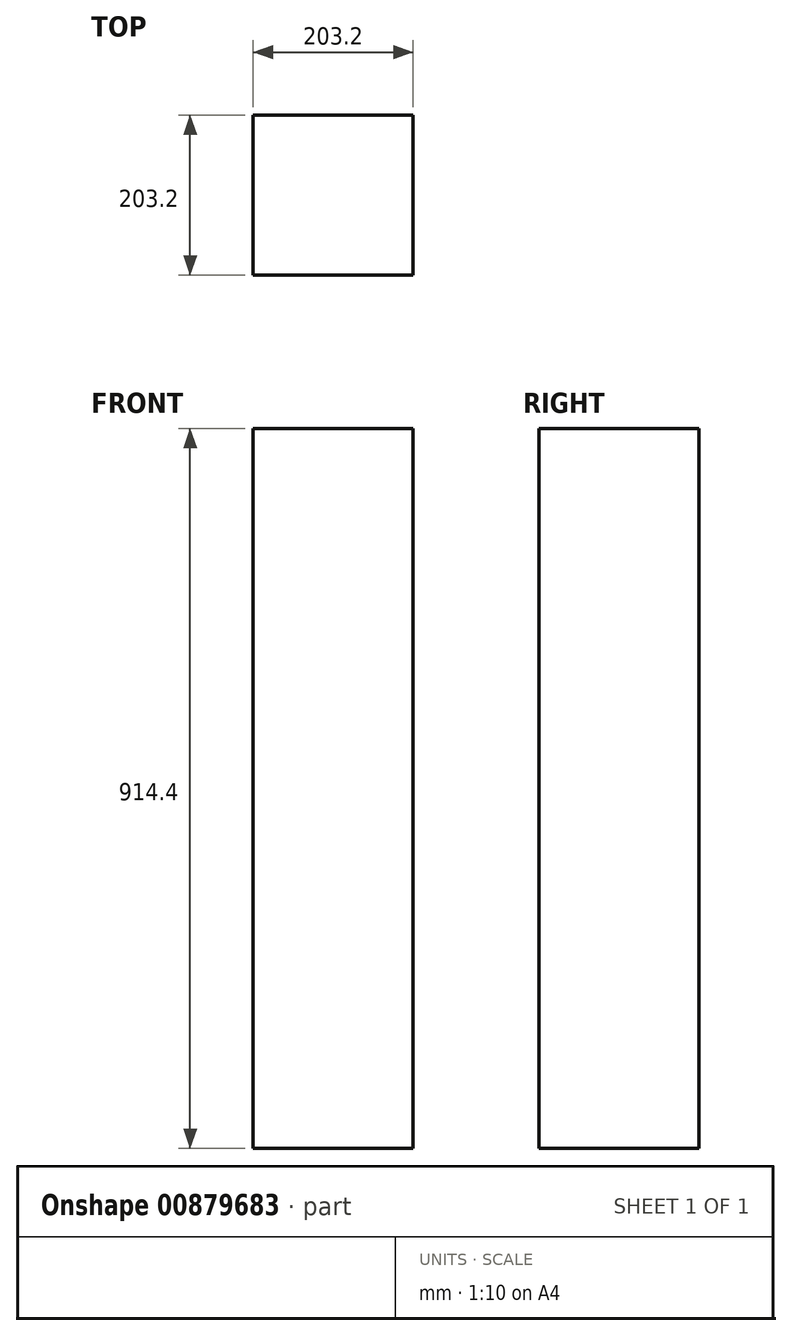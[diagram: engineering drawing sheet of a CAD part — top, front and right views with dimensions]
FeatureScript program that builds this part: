
annotation { "Feature Type Name" : "Feature", "Feature Type Description" : "" }
export const myFeature = defineFeature(function(context is Context, id is Id, definition is map)
    precondition{}
    {
        {
            var Q0;
            Q0=qCreatedBy(makeId("Top.planeOp"),FACE);
            var sketch = newSketch(context, id + "F0", { "sketchPlane" : qUnion([Q0])});
            skLineSegment(sketch, "E0.bottom", {"start": v(-99.17, 115.85) * mm, "end": v(104.03, 115.85) * mm});
            skLineSegment(sketch, "E0.top", {"start": v(-99.17, -87.35) * mm, "end": v(104.03, -87.35) * mm});
            skLineSegment(sketch, "E0.left", {"start": v(-99.17, 115.85) * mm, "end": v(-99.17, -87.35) * mm});
            skLineSegment(sketch, "E0.right", {"start": v(104.03, 115.85) * mm, "end": v(104.03, -87.35) * mm});
            skSolve(sketch);
        }
        {
            var Q0;
            Q0=makeQuery(id+"F0.imprint","IMPRINT",FACE,{"disambiguationData":[TD([[makeQuery(id+"F0.imprint","IMPRINT",EDGE,{"derivedFrom":sQuery(id+"F0.wireOp",EDGE,"E0.bottom")}),-1.0]])]});
            extrude(context, id + "F1", {"entities" : qUnion([Q0]), "depth" : 914.4 * mm, "offsetDistance" : 25.4 * mm});
        }
    });
